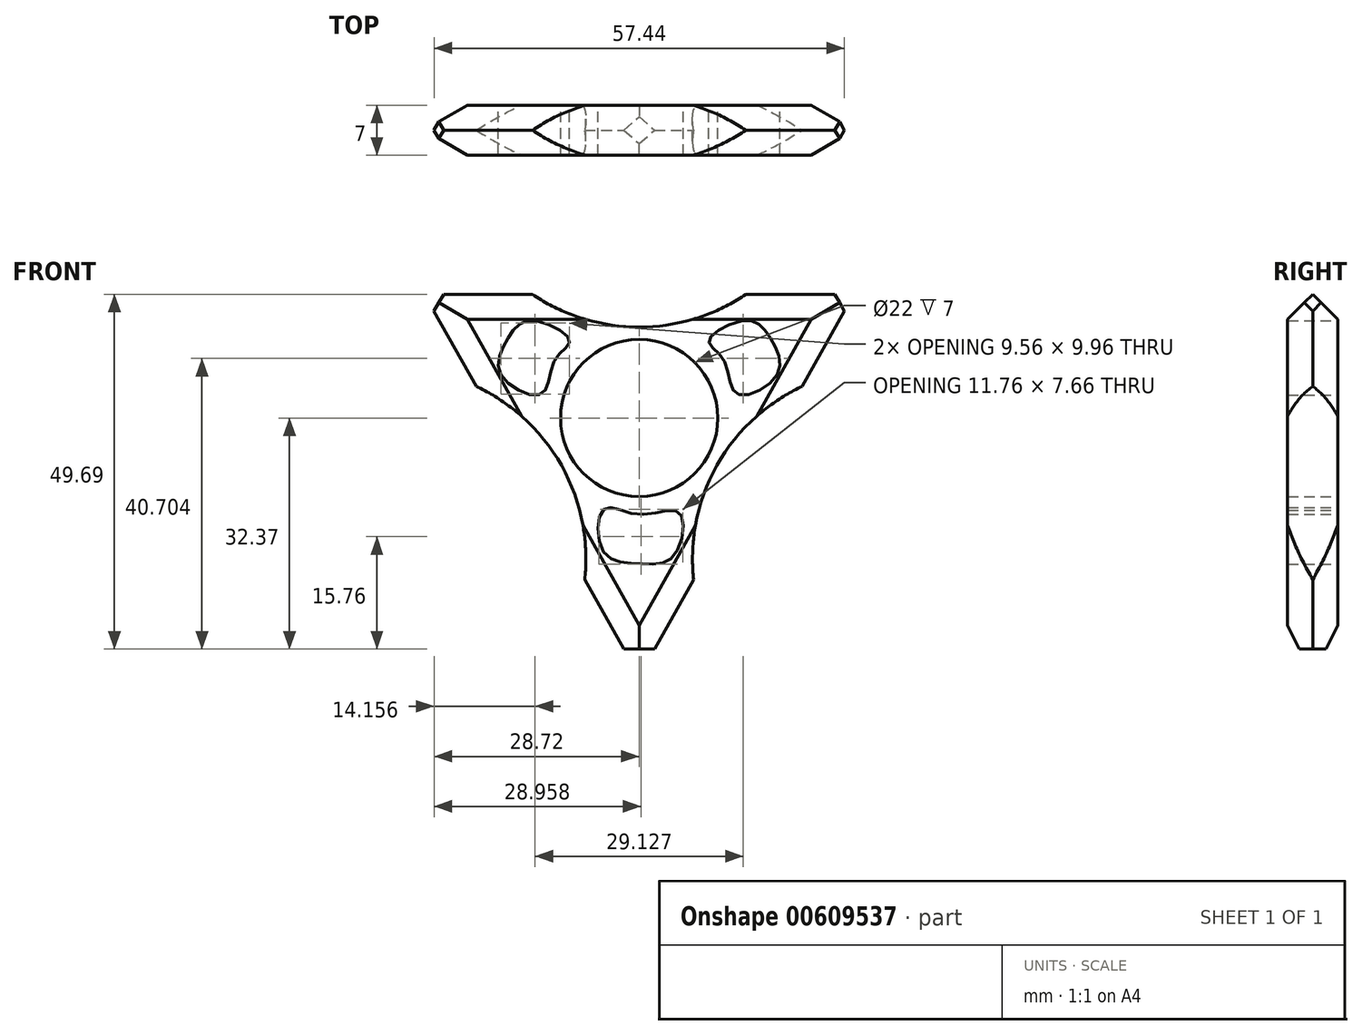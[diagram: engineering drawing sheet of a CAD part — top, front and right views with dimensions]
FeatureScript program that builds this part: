
annotation { "Feature Type Name" : "Feature", "Feature Type Description" : "" }
export const myFeature = defineFeature(function(context is Context, id is Id, definition is map)
    precondition{}
    {
        {
            var Q0;
            Q0=qCreatedBy(makeId("Front.planeOp"),FACE);
            var sketch = newSketch(context, id + "F0", { "sketchPlane" : qUnion([Q0])});
            skLineSegment(sketch, "E0.0", {"start": v(0, -39.41) * mm, "end": v(-32.73, 18.9) * mm});
            skLineSegment(sketch, "E0.1", {"start": v(-32.73, 18.9) * mm, "end": v(32.73, 18.9) * mm});
            skLineSegment(sketch, "E0.2", {"start": v(32.73, 18.9) * mm, "end": v(0, -39.41) * mm});
            skPoint(sketch, "E0.0.midPoint", {"position": v(-16.37, -10.26) * mm});
            skCircle(sketch, "E1", {"center": v(0, 39.41) * mm, "radius": 26.67 * mm});
            skCircle(sketch, "E2", {"center": v(-34.13, -19.7) * mm, "radius": 26.67 * mm});
            skCircle(sketch, "E3", {"center": v(34.13, -19.7) * mm, "radius": 26.67 * mm});
            skLineSegment(sketch, "E4.1", {"start": v(18.69, 32.37) * mm, "end": v(37.38, 0) * mm});
            skLineSegment(sketch, "E4.3", {"start": v(18.69, -32.37) * mm, "end": v(-18.69, -32.37) * mm});
            skLineSegment(sketch, "E4.5", {"start": v(-37.38, 0) * mm, "end": v(-18.69, 32.37) * mm});
            skPoint(sketch, "E4.0.midPoint", {"position": v(0, 32.37) * mm});
            skCircle(sketch, "E5", {"center": v(0, 0) * mm, "radius": 11 * mm});
            skFitSpline(sketch, "E6", {"points": [v(-19.34, 6.06) * mm, v(-13.67, 3.4) * mm, v(-11.83, 8.14) * mm, v(-9.75, 10.87) * mm, v(-15.15, 13.66) * mm, v(-18.44, 11.07) * mm, v(-19.34, 6.06) * mm]});
            skFitSpline(sketch, "E7.MirrorC", {"points": [v(19.34, 6.06) * mm, v(13.67, 3.4) * mm, v(11.83, 8.14) * mm, v(9.75, 10.87) * mm, v(15.15, 13.66) * mm, v(18.44, 11.07) * mm, v(19.34, 6.06) * mm]});
            skFitSpline(sketch, "E8", {"points": [v(-4.97, -12.78) * mm, v(0, -13.5) * mm, v(5.6, -13.26) * mm, v(4.88, -19.26) * mm, v(0.1, -20.4) * mm, v(-4.97, -18.78) * mm, v(-4.97, -12.78) * mm]});
            skSolve(sketch);
        }
        {
            var Q0;
            Q0=makeQuery(id+"F0.imprint","IMPRINT",FACE,{"disambiguationData":[TD([[makeQuery(id+"F0.imprint","IMPRINT",EDGE,{"derivedFrom":sQuery(id+"F0.wireOp",EDGE,"E5")}),-1.0]])]});
            extrude(context, id + "F1", {"entities" : qUnion([Q0]), "depth" : 7 * mm, "offsetDistance" : 25.4 * mm});
        }
        {
            var Q0;
            {var subQ0=sQuery(id+"F0.wireOp",EDGE,"E0.0");Q0=makeQuery(id+"F1.opExtrude","CAP_EDGE",EDGE,{"disambiguationData":[OSD([subQ0]),TDD([makeQuery(id+"F0.imprint","IMPRINT",EDGE,{"disambiguationData":[TD([[makeQuery(id+"F0.imprint","INTERSECT",VERTEX,{"derivedFrom":[subQ0,sQuery(id+"F0.wireOp",EDGE,"E4.5")]}),1.0]])],"derivedFrom":subQ0})])],"isStart":false});}
            var Q1;
            {var subQ0=sQuery(id+"F0.wireOp",EDGE,"E0.1");Q1=makeQuery(id+"F1.opExtrude","CAP_EDGE",EDGE,{"disambiguationData":[OSD([subQ0]),TDD([makeQuery(id+"F0.imprint","IMPRINT",EDGE,{"disambiguationData":[TD([[makeQuery(id+"F0.imprint","INTERSECT",VERTEX,{"derivedFrom":[subQ0,sQuery(id+"F0.wireOp",EDGE,"E4.5")]}),-1.0]])],"derivedFrom":subQ0})])],"isStart":false});}
            var Q2;
            {var subQ0=sQuery(id+"F0.wireOp",EDGE,"E0.2");Q2=makeQuery(id+"F1.opExtrude","CAP_EDGE",EDGE,{"disambiguationData":[OSD([subQ0]),TDD([makeQuery(id+"F0.imprint","IMPRINT",EDGE,{"disambiguationData":[TD([[makeQuery(id+"F0.imprint","INTERSECT",VERTEX,{"derivedFrom":[subQ0,sQuery(id+"F0.wireOp",EDGE,"E4.3")]}),1.0]])],"derivedFrom":subQ0})])],"isStart":false});}
            var Q3;
            {var subQ0=sQuery(id+"F0.wireOp",EDGE,"E0.0");Q3=makeQuery(id+"F1.opExtrude","CAP_EDGE",EDGE,{"disambiguationData":[OSD([subQ0]),TDD([makeQuery(id+"F0.imprint","IMPRINT",EDGE,{"disambiguationData":[TD([[makeQuery(id+"F0.imprint","INTERSECT",VERTEX,{"derivedFrom":[subQ0,sQuery(id+"F0.wireOp",EDGE,"E4.3")]}),-1.0]])],"derivedFrom":subQ0})])],"isStart":false});}
            var Q4;
            {var subQ0=sQuery(id+"F0.wireOp",EDGE,"E0.2");Q4=makeQuery(id+"F1.opExtrude","CAP_EDGE",EDGE,{"disambiguationData":[OSD([subQ0]),TDD([makeQuery(id+"F0.imprint","IMPRINT",EDGE,{"disambiguationData":[TD([[makeQuery(id+"F0.imprint","INTERSECT",VERTEX,{"derivedFrom":[subQ0,sQuery(id+"F0.wireOp",EDGE,"E4.1")]}),-1.0]])],"derivedFrom":subQ0})])],"isStart":false});}
            var Q5;
            {var subQ0=sQuery(id+"F0.wireOp",EDGE,"E0.1");Q5=makeQuery(id+"F1.opExtrude","CAP_EDGE",EDGE,{"disambiguationData":[OSD([subQ0]),TDD([makeQuery(id+"F0.imprint","IMPRINT",EDGE,{"disambiguationData":[TD([[makeQuery(id+"F0.imprint","INTERSECT",VERTEX,{"derivedFrom":[subQ0,sQuery(id+"F0.wireOp",EDGE,"E4.1")]}),1.0]])],"derivedFrom":subQ0})])],"isStart":false});}
            var Q6;
            {var subQ0=sQuery(id+"F0.wireOp",EDGE,"E0.0");Q6=makeQuery(id+"F1.opExtrude","CAP_EDGE",EDGE,{"disambiguationData":[OSD([subQ0]),TDD([makeQuery(id+"F0.imprint","IMPRINT",EDGE,{"disambiguationData":[TD([[makeQuery(id+"F0.imprint","INTERSECT",VERTEX,{"derivedFrom":[subQ0,sQuery(id+"F0.wireOp",EDGE,"E4.3")]}),-1.0]])],"derivedFrom":subQ0})])],"isStart":true});}
            var Q7;
            {var subQ0=sQuery(id+"F0.wireOp",EDGE,"E0.2");Q7=makeQuery(id+"F1.opExtrude","CAP_EDGE",EDGE,{"disambiguationData":[OSD([subQ0]),TDD([makeQuery(id+"F0.imprint","IMPRINT",EDGE,{"disambiguationData":[TD([[makeQuery(id+"F0.imprint","INTERSECT",VERTEX,{"derivedFrom":[subQ0,sQuery(id+"F0.wireOp",EDGE,"E4.3")]}),1.0]])],"derivedFrom":subQ0})])],"isStart":true});}
            var Q8;
            {var subQ0=sQuery(id+"F0.wireOp",EDGE,"E0.2");Q8=makeQuery(id+"F1.opExtrude","CAP_EDGE",EDGE,{"disambiguationData":[OSD([subQ0]),TDD([makeQuery(id+"F0.imprint","IMPRINT",EDGE,{"disambiguationData":[TD([[makeQuery(id+"F0.imprint","INTERSECT",VERTEX,{"derivedFrom":[subQ0,sQuery(id+"F0.wireOp",EDGE,"E4.1")]}),-1.0]])],"derivedFrom":subQ0})])],"isStart":true});}
            var Q9;
            {var subQ0=sQuery(id+"F0.wireOp",EDGE,"E0.1");Q9=makeQuery(id+"F1.opExtrude","CAP_EDGE",EDGE,{"disambiguationData":[OSD([subQ0]),TDD([makeQuery(id+"F0.imprint","IMPRINT",EDGE,{"disambiguationData":[TD([[makeQuery(id+"F0.imprint","INTERSECT",VERTEX,{"derivedFrom":[subQ0,sQuery(id+"F0.wireOp",EDGE,"E4.1")]}),1.0]])],"derivedFrom":subQ0})])],"isStart":true});}
            var Q10;
            {var subQ0=sQuery(id+"F0.wireOp",EDGE,"E0.1");Q10=makeQuery(id+"F1.opExtrude","CAP_EDGE",EDGE,{"disambiguationData":[OSD([subQ0]),TDD([makeQuery(id+"F0.imprint","IMPRINT",EDGE,{"disambiguationData":[TD([[makeQuery(id+"F0.imprint","INTERSECT",VERTEX,{"derivedFrom":[subQ0,sQuery(id+"F0.wireOp",EDGE,"E4.5")]}),-1.0]])],"derivedFrom":subQ0})])],"isStart":true});}
            var Q11;
            {var subQ0=sQuery(id+"F0.wireOp",EDGE,"E0.0");Q11=makeQuery(id+"F1.opExtrude","CAP_EDGE",EDGE,{"disambiguationData":[OSD([subQ0]),TDD([makeQuery(id+"F0.imprint","IMPRINT",EDGE,{"disambiguationData":[TD([[makeQuery(id+"F0.imprint","INTERSECT",VERTEX,{"derivedFrom":[subQ0,sQuery(id+"F0.wireOp",EDGE,"E4.5")]}),1.0]])],"derivedFrom":subQ0})])],"isStart":true});}
            chamfer(context, id + "F2", {"entities" : qUnion([Q0, Q1, Q2, Q3, Q4, Q5, Q6, Q7, Q8, Q9, Q10, Q11]), "width" : 5.08 * mm, "tangentPropagation" : true});
        }
    });
